# Revit family: 306_H6_SP
name_source: partatom
category: Pipe Accessories
units: mm (PartAtom-declared; Revit-internal decimal feet)

## family parameters
Always vertical = Yes
Cut with Voids When Loaded = No
Part Type = Valve - Breaks Into
Round Connector Dimension = Use Diameter
Shared = No
Work Plane-Based = No

## types (7) — shared parameters
CAT0 = Yes
CenSd_NR_6 = 26 mm  [stored 0.0853018 ft]
Description = Globe valve, partial pressure relief, 2-way, Flange, PN 16
L2D_Min = 3048 mm
Manufacturer = Belimo
NR = 30 mm  [stored 0.0984252 ft]
QmdConnectorList = 301;D;302;D
magiPartTypeId = 306
magiProductFamilyId = H6*SP
zero-valued in all types: MC_Default_elevation

## per-type parameters (varying)
| type | C | C__ve | D | DD1 | DD2 | DR | FD | HH | HH1 | HH1__ve | HH2 | HH3 | HH4 | HH4__ve | HH5 | L2 | L2D | L4 | L42 | LL1 | LM | W2D |
| H640SP | 18 mm  [stored 0.0590551 ft] | -18 mm  [stored -0.0590551 ft] | 40 mm | 60 mm | 105 mm | 38 mm | 150 mm | 68 mm | 14 mm  [stored 0.0459318 ft] | -14 mm | 41 mm | 54 mm | 60 mm | -60 mm  [stored -0.19685 ft] | 27 mm | 100 mm | 200 mm | 50 mm | 41 mm | 65 mm | 164 mm | 40 mm  [stored 0.131234 ft] |
| H6150SP | 26 mm  [stored 0.0853018 ft] | -26 mm  [stored -0.0853018 ft] | 150 mm | 114 mm | 200 mm | 71 mm | 285 mm | 153 mm | 31 mm  [stored 0.101706 ft] | -31 mm | 92 mm | 122 mm | 114 mm | -114 mm  [stored -0.374016 ft] | 61 mm | 240 mm | 480 mm | 120 mm | 78 mm | 145 mm | 428 mm | 150 mm |
| H6125SP | 26 mm  [stored 0.0853018 ft] | -26 mm  [stored -0.0853018 ft] | 125 mm | 100 mm | 175 mm | 63 mm | 250 mm | 123 mm | 25 mm  [stored 0.082021 ft] | -25 mm  [stored -0.082021 ft] | 74 mm | 98 mm | 100 mm | -100 mm  [stored -0.328084 ft] | 49 mm | 200 mm | 400 mm | 100 mm | 69 mm | 125 mm | 348 mm | 125 mm |
| H6100SP | 24 mm  [stored 0.0787402 ft] | -24 mm  [stored -0.0787402 ft] | 100 mm | 88 mm | 154 mm | 55 mm | 220 mm | 97 mm | 19 mm | -19 mm | 58 mm | 77 mm | 88 mm | -88 mm  [stored -0.288714 ft] | 39 mm | 175 mm | 350 mm | 88 mm | 61 mm | 103 mm | 302 mm | 100 mm |
| H679SP | 22 mm  [stored 0.0721785 ft] | -22 mm  [stored -0.0721785 ft] | 80 mm | 80 mm | 140 mm | 50 mm | 200 mm | 87 mm | 17 mm | -17 mm | 52 mm | 69 mm | 80 mm | -80 mm  [stored -0.262467 ft] | 35 mm | 155 mm | 310 mm | 78 mm | 55 mm | 93 mm | 266 mm | 80 mm |
| H664SP | 20 mm  [stored 0.0656168 ft] | -20 mm  [stored -0.0656168 ft] | 65 mm | 74 mm | 130 mm | 46 mm | 185 mm | 78 mm | 16 mm | -16 mm | 47 mm | 62 mm | 74 mm | -74 mm  [stored -0.242782 ft] | 31 mm  [stored 0.101706 ft] | 145 mm | 290 mm | 73 mm | 51 mm | 88 mm | 250 mm | 65 mm |
| H650SP | 20 mm  [stored 0.0656168 ft] | -20 mm  [stored -0.0656168 ft] | 50 mm | 66 mm | 116 mm | 41 mm | 165 mm | 71 mm | 14 mm  [stored 0.0459318 ft] | -14 mm | 43 mm | 57 mm | 66 mm | -66 mm  [stored -0.216535 ft] | 28 mm | 115 mm | 230 mm | 58 mm | 45 mm | 73 mm | 190 mm | 50 mm |

note: column(s) folded — value = type name in every type: magiProductCode, magiProductId

note: [stored X ft] marks values corroborated as IEEE doubles in the binary element streams (Revit-internal decimal feet)

## geometry (parser evidence)
native form markers: Sweep x2
no freeform markers — native parametric forms only
